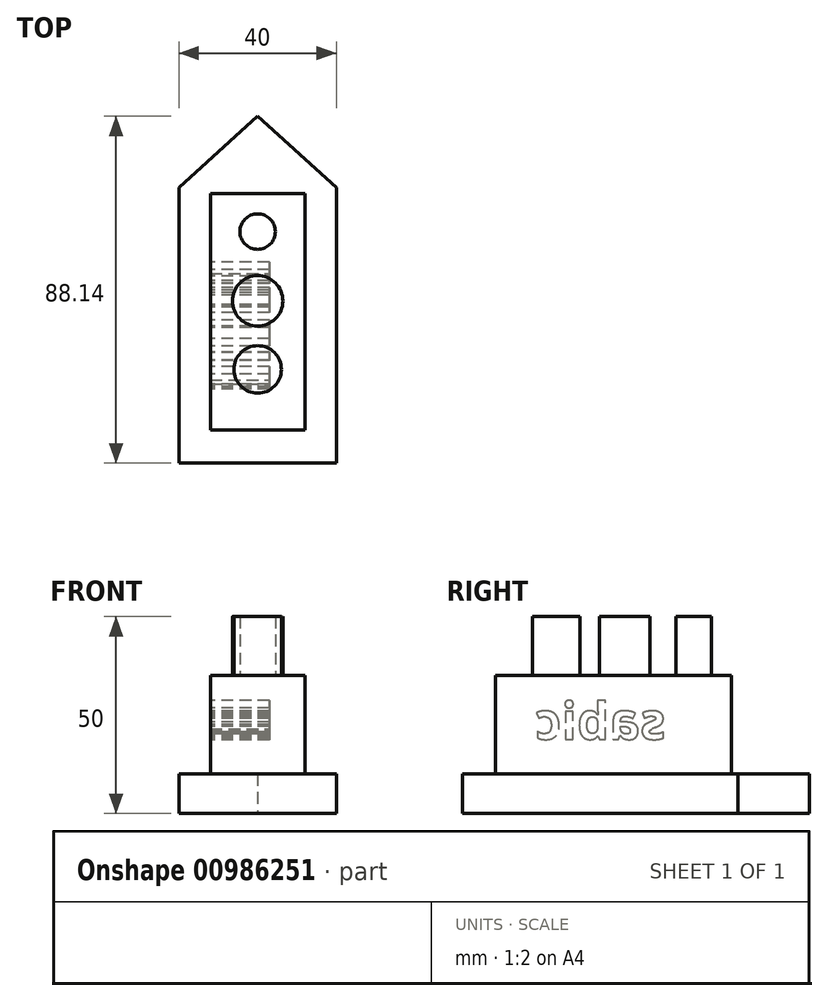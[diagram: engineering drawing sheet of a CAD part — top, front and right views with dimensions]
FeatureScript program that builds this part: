
annotation { "Feature Type Name" : "Feature", "Feature Type Description" : "" }
export const myFeature = defineFeature(function(context is Context, id is Id, definition is map)
    precondition{}
    {
        {
            var Q0;
            Q0=qCreatedBy(makeId("Top.planeOp"),FACE);
            var sketch = newSketch(context, id + "F0", { "sketchPlane" : qUnion([Q0])});
            skLineSegment(sketch, "E0", {"start": v(-20, 32.99) * mm, "end": v(-20, -37.01) * mm});
            skLineSegment(sketch, "E1", {"start": v(-20, -37.01) * mm, "end": v(20, -37.01) * mm});
            skLineSegment(sketch, "E2", {"start": v(20, -37.01) * mm, "end": v(20, 32.99) * mm});
            skLineSegment(sketch, "E3", {"start": v(-20, 32.99) * mm, "end": v(0, 51.13) * mm});
            skLineSegment(sketch, "E4", {"start": v(20, 32.99) * mm, "end": v(0, 51.13) * mm});
            skSolve(sketch);
        }
        {
            var Q0;
            Q0 = qSketchRegion(id + "F0", true);
            extrude(context, id + "F1", {"entities" : qUnion([Q0]), "depth" : 10 * mm, "offsetDistance" : 25 * mm});
        }
        {
            var Q0;
            Q0=makeQuery(id+"F1.opExtrude","CAP_FACE",FACE,{"disambiguationData":[OSD([sQuery(id+"F0.wireOp",EDGE,"E0"),sQuery(id+"F0.wireOp",EDGE,"E1"),sQuery(id+"F0.wireOp",EDGE,"E2"),sQuery(id+"F0.wireOp",EDGE,"E3"),sQuery(id+"F0.wireOp",EDGE,"E4")])],"isStart":false});
            var sketch = newSketch(context, id + "F2", { "sketchPlane" : qUnion([Q0])});
            skLineSegment(sketch, "E5.bottom", {"start": v(12, 31.42) * mm, "end": v(-12, 31.42) * mm});
            skLineSegment(sketch, "E5.top", {"start": v(12, -28.58) * mm, "end": v(-12, -28.58) * mm});
            skLineSegment(sketch, "E5.left", {"start": v(12, 31.42) * mm, "end": v(12, -28.58) * mm});
            skLineSegment(sketch, "E5.right", {"start": v(-12, 31.42) * mm, "end": v(-12, -28.58) * mm});
            skSolve(sketch);
        }
        {
            var Q0;
            Q0=makeQuery(id+"F2.imprint","IMPRINT",FACE,{"disambiguationData":[TD([[makeQuery(id+"F2.imprint","IMPRINT",EDGE,{"derivedFrom":sQuery(id+"F2.wireOp",EDGE,"E5.bottom")}),1.0]])]});
            var sketch = newSketch(context, id + "F3", { "sketchPlane" : qUnion([Q0])});
            skSolve(sketch);
        }
        {
            var Q0;
            Q0=makeQuery(id+"F2.imprint","IMPRINT",FACE,{"disambiguationData":[TD([[makeQuery(id+"F2.imprint","IMPRINT",EDGE,{"derivedFrom":sQuery(id+"F2.wireOp",EDGE,"E5.bottom")}),1.0]])]});
            extrude(context, id + "F4", {"entities" : qUnion([Q0]), "operationType" : NewBodyOperationType.ADD, "depth" : 25 * mm, "offsetDistance" : 25 * mm});
        }
        {
            var Q0;
            Q0=makeQuery(id+"F4.opExtrude","CAP_FACE",FACE,{"disambiguationData":[OSD([sQuery(id+"F2.wireOp",EDGE,"E5.bottom"),sQuery(id+"F2.wireOp",EDGE,"E5.top"),sQuery(id+"F2.wireOp",EDGE,"E5.left"),sQuery(id+"F2.wireOp",EDGE,"E5.right")])],"isStart":false});
            var sketch = newSketch(context, id + "F5", { "sketchPlane" : qUnion([Q0])});
            skCircle(sketch, "E6", {"center": v(0, 21.8) * mm, "radius": 4.5 * mm});
            skCircle(sketch, "E7", {"center": v(0, 4.2) * mm, "radius": 6.4 * mm});
            skCircle(sketch, "E8", {"center": v(0, -13.22) * mm, "radius": 6.03 * mm});
            skSolve(sketch);
        }
        {
            var Q0;
            Q0 = qSketchRegion(id + "F5", true);
            extrude(context, id + "F6", {"entities" : qUnion([Q0]), "depth" : 15 * mm, "offsetDistance" : 25 * mm});
        }
        {
            var Q0;
            Q0=makeQuery(id+"F4.opExtrude","SWEPT_FACE",FACE,{"disambiguationData":[OSD([sQuery(id+"F2.wireOp",EDGE,"E5.right")])]});
            var sketch = newSketch(context, id + "F7", { "sketchPlane" : qUnion([Q0])});
            skText(sketch, "E9", { "text": " sabic", "fontName": "OpenSans-Bold.ttf"});
            const initialGuessF7  = {"E9": [-0.01799, 0.01884, 1, 0, 0.00935]};
            skSetInitialGuess(sketch, initialGuessF7);
            skSolve(sketch);
        }
        {
            var Q0;
            Q0 = qSketchRegion(id + "F7", true);
            extrude(context, id + "F8", {"entities" : qUnion([Q0]), "operationType" : NewBodyOperationType.REMOVE, "oppositeDirection" : true, "depth" : 15 * mm, "offsetDistance" : 25 * mm});
        }
    });
